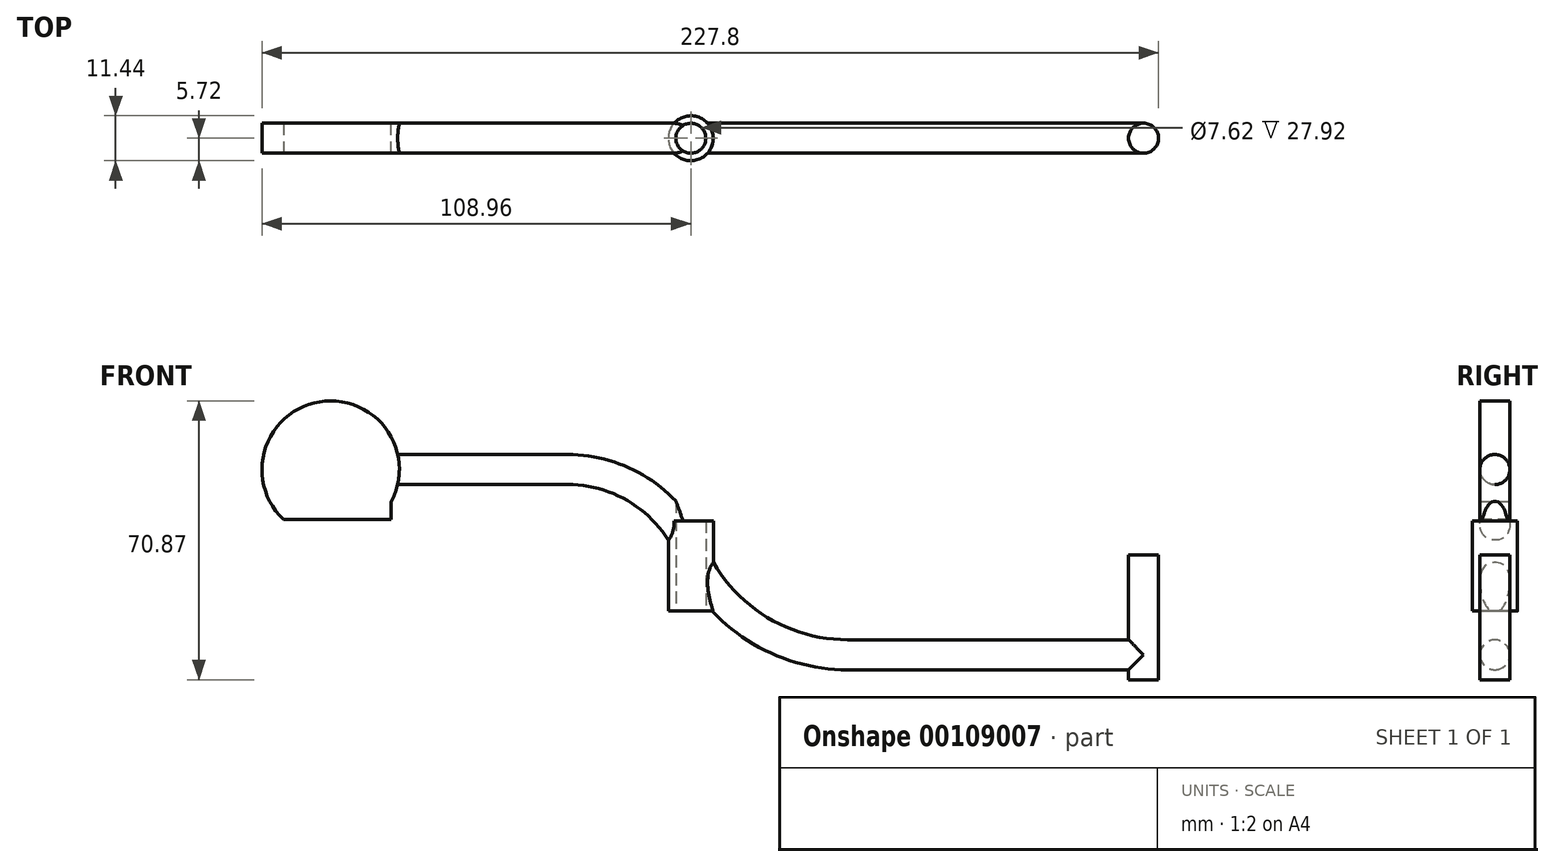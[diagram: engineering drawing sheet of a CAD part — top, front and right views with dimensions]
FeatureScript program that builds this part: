
annotation { "Feature Type Name" : "Feature", "Feature Type Description" : "" }
export const myFeature = defineFeature(function(context is Context, id is Id, definition is map)
    precondition{}
    {
        {
            var Q0;
            Q0=qCreatedBy(makeId("Front.planeOp"),FACE);
            var sketch = newSketch(context, id + "F0", { "sketchPlane" : qUnion([Q0])});
            skLineSegment(sketch, "E0", {"start": v(-106.83, 20.7) * mm, "end": v(-31.27, 20.7) * mm});
            skArc(sketch, "E1", {"start": v(-31.27, 20.7) * mm, "mid": v(-12.52, 15.05) * mm, "end": v(0, 0) * mm});
            skArc(sketch, "E2", {"start": v(0, 0) * mm, "mid": v(15.95, -19.18) * mm, "end": v(39.84, -26.37) * mm});
            skLineSegment(sketch, "E3", {"start": v(39.84, -26.37) * mm, "end": v(115.03, -26.37) * mm});
            skSolve(sketch);
        }
        {
            var Q0;
            Q0=sQuery(id+"F0.wireOp",EDGE,"E0");
            var Q1;
            Q1=sQuery(id+"F0.wireOp",VERTEX,"E0.start");
            cPlane(context, id + "F1", {"entities" : qUnion([Q0, Q1]), "cplaneType" : CPlaneType.LINE_POINT, "offset" : 25.4 * mm, "width" : 152.4 * mm, "height" : 152.4 * mm});
        }
        {
            var Q0;
            Q0=qCreatedBy(id+"F1.planeOp",FACE);
            var sketch = newSketch(context, id + "F2", { "sketchPlane" : qUnion([Q0])});
            skCircle(sketch, "E4", {"center": v(0, 20.7) * mm, "radius": 3.81 * mm});
            skSolve(sketch);
        }
        {
            var Q0;
            Q0=makeQuery(id+"F2.imprint","IMPRINT",FACE,{"disambiguationData":[TD([[makeQuery(id+"F2.imprint","IMPRINT",EDGE,{"derivedFrom":sQuery(id+"F2.wireOp",EDGE,"E4")}),1.0]])]});
            var Q1;
            Q1=sQuery(id+"F0.wireOp",EDGE,"E0");
            var Q2;
            Q2=sQuery(id+"F0.wireOp",EDGE,"E1");
            var Q3;
            Q3=sQuery(id+"F0.wireOp",EDGE,"E2");
            var Q4;
            Q4=sQuery(id+"F0.wireOp",EDGE,"E3");
            sweep(context, id + "F3", {"profiles" : qUnion([Q0]), "path" : qUnion([Q1, Q2, Q3, Q4])});
        }
        {
            var Q0;
            Q0=qCreatedBy(makeId("Top.planeOp"),FACE);
            var sketch = newSketch(context, id + "F4", { "sketchPlane" : qUnion([Q0])});
            skCircle(sketch, "E5", {"center": v(0, 0) * mm, "radius": 3.81 * mm});
            skCircle(sketch, "E6", {"center": v(0, 0) * mm, "radius": 5.72 * mm});
            skSolve(sketch);
        }
        {
            var Q0;
            Q0=makeQuery(id+"F4.imprint","IMPRINT",FACE,{"disambiguationData":[TD([[makeQuery(id+"F4.imprint","IMPRINT",EDGE,{"derivedFrom":sQuery(id+"F4.wireOp",EDGE,"E5")}),1.0]])]});
            extrude(context, id + "F5", {"entities" : qUnion([Q0]), "operationType" : NewBodyOperationType.REMOVE, "depth" : 25.4 * mm, "hasSecondDirection" : true, "secondDirectionOppositeDirection" : true, "secondDirectionDepth" : 25.4 * mm});
        }
        {
            var Q0;
            Q0=makeQuery(id+"F4.imprint","IMPRINT",FACE,{"disambiguationData":[TD([[makeQuery(id+"F4.imprint","IMPRINT",EDGE,{"derivedFrom":sQuery(id+"F4.wireOp",EDGE,"E5")}),-1.0]])]});
            extrude(context, id + "F6", {"entities" : qUnion([Q0]), "operationType" : NewBodyOperationType.ADD, "depth" : 7.62 * mm, "hasSecondDirection" : true, "secondDirectionOppositeDirection" : true, "secondDirectionDepth" : 15.24 * mm});
        }
        {
            var Q0;
            Q0=sQuery(id+"F0.wireOp",EDGE,"E3");
            cPlane(context, id + "F7", {"entities" : qUnion([Q0]), "cplaneType" : CPlaneType.LINE_ANGLE, "offset" : 25.4 * mm, "angle" : 90 * degree, "width" : 152.4 * mm, "height" : 152.4 * mm});
        }
        {
            var Q0;
            Q0=qCreatedBy(id+"F7.planeOp",FACE);
            var sketch = newSketch(context, id + "F8", { "sketchPlane" : qUnion([Q0])});
            skCircle(sketch, "E7", {"center": v(115.03, 0) * mm, "radius": 3.81 * mm});
            skSolve(sketch);
        }
        {
            var Q0;
            Q0=makeQuery(id+"F8.imprint","IMPRINT",FACE,{"disambiguationData":[TD([[makeQuery(id+"F8.imprint","IMPRINT",EDGE,{"derivedFrom":sQuery(id+"F8.wireOp",EDGE,"E7")}),1.0]])]});
            extrude(context, id + "F9", {"entities" : qUnion([Q0]), "operationType" : NewBodyOperationType.ADD, "depth" : 25.4 * mm, "hasSecondDirection" : true, "secondDirectionOppositeDirection" : true, "secondDirectionDepth" : 6.35 * mm});
        }
        {
            var Q0;
            Q0=qCreatedBy(makeId("Front.planeOp"),FACE);
            var sketch = newSketch(context, id + "F10", { "sketchPlane" : qUnion([Q0])});
            skLineSegment(sketch, "E8", {"start": v(-76.08, 20.7) * mm, "end": v(-76.08, 33.4) * mm});
            skLineSegment(sketch, "E9", {"start": v(-76.08, 33.4) * mm, "end": v(-106.91, 33.4) * mm});
            skLineSegment(sketch, "E10", {"start": v(-106.91, 33.4) * mm, "end": v(-106.91, 8) * mm});
            skLineSegment(sketch, "E11", {"start": v(-106.91, 8) * mm, "end": v(-76.08, 8) * mm});
            skLineSegment(sketch, "E12", {"start": v(-76.08, 8) * mm, "end": v(-76.08, 20.7) * mm});
            skSolve(sketch);
        }
        {
            var Q0;
            Q0=makeQuery(id+"F10.imprint","IMPRINT",FACE,{"disambiguationData":[TD([[makeQuery(id+"F10.imprint","IMPRINT",EDGE,{"derivedFrom":sQuery(id+"F10.wireOp",EDGE,"E8")}),1.0]])]});
            extrude(context, id + "F11", {"entities" : qUnion([Q0]), "operationType" : NewBodyOperationType.ADD, "depth" : 3.8 * mm, "hasSecondDirection" : true, "secondDirectionOppositeDirection" : true, "secondDirectionDepth" : 3.8 * mm});
        }
        {
            var Q0;
            Q0=makeQuery(id+"F11.opExtrude","CAP_FACE",FACE,{"disambiguationData":[OSD([sQuery(id+"F10.wireOp",EDGE,"E8"),sQuery(id+"F10.wireOp",EDGE,"E9"),sQuery(id+"F10.wireOp",EDGE,"E10"),sQuery(id+"F10.wireOp",EDGE,"E11"),sQuery(id+"F10.wireOp",EDGE,"E12")])],"isStart":false});
            var sketch = newSketch(context, id + "F12", { "sketchPlane" : qUnion([Q0])});
            skCircle(sketch, "E13", {"center": v(-91.5, 20.7) * mm, "radius": 17.46 * mm});
            skSolve(sketch);
        }
        {
            var Q0;
            {var subQ0=sQuery(id+"F12.wireOp",EDGE,"E13");var subQ1=makeQuery(id+"F11.opExtrude","CAP_EDGE",EDGE,{"disambiguationData":[OSD([sQuery(id+"F10.wireOp",EDGE,"E9")])],"isStart":false});var subQ2=makeQuery(id+"F12.imprint","INTERSECT",VERTEX,{"disambiguationData":[OD(0.0)],"derivedFrom":[subQ1,subQ0]});Q0=makeQuery(id+"F12.imprint","IMPRINT",FACE,{"disambiguationData":[TD([[makeQuery(id+"F12.imprint","IMPRINT",EDGE,{"disambiguationData":[TD([[subQ2,-1.0]])],"derivedFrom":subQ0}),1.0]])]});}
            var Q1;
            {var subQ0=sQuery(id+"F12.wireOp",EDGE,"E13");var subQ2=sQuery(id+"F10.wireOp",EDGE,"E12");var subQ4=sQuery(id+"F10.wireOp",EDGE,"E9");var subQ5=sQuery(id+"F10.wireOp",EDGE,"E8");var subQ8=makeQuery(id+"F11.opExtrude","CAP_EDGE",EDGE,{"disambiguationData":[OSD([subQ5,subQ2])],"isStart":false});var subQ9=makeQuery(id+"F11.boolean.opBoolean","SPLIT",EDGE,{"disambiguationData":[TD([makeQuery(id+"F11.opExtrude","SWEPT_FACE",FACE,{"disambiguationData":[OSD([subQ4])]})])],"derivedFrom":subQ8});var subQ10=makeQuery(id+"F12.imprint","INTERSECT",VERTEX,{"derivedFrom":[subQ9,subQ0]});Q1=makeQuery(id+"F12.imprint","IMPRINT",FACE,{"disambiguationData":[TD([[makeQuery(id+"F12.imprint","IMPRINT",EDGE,{"disambiguationData":[TD([[subQ10,1.0]])],"derivedFrom":subQ0}),1.0]])]});}
            var Q2;
            {var subQ0=sQuery(id+"F12.wireOp",EDGE,"E13");var subQ1=makeQuery(id+"F11.opExtrude","CAP_EDGE",EDGE,{"disambiguationData":[OSD([sQuery(id+"F10.wireOp",EDGE,"E11")])],"isStart":false});var subQ2=makeQuery(id+"F12.imprint","INTERSECT",VERTEX,{"disambiguationData":[OD(0.0)],"derivedFrom":[subQ1,subQ0]});Q2=makeQuery(id+"F12.imprint","IMPRINT",FACE,{"disambiguationData":[TD([[makeQuery(id+"F12.imprint","IMPRINT",EDGE,{"disambiguationData":[TD([[subQ2,-1.0]])],"derivedFrom":subQ0}),1.0]])]});}
            var Q3;
            {var subQ0=sQuery(id+"F12.wireOp",EDGE,"E13");var subQ1=makeQuery(id+"F11.opExtrude","CAP_EDGE",EDGE,{"disambiguationData":[OSD([sQuery(id+"F10.wireOp",EDGE,"E10")])],"isStart":false});var subQ2=makeQuery(id+"F12.imprint","INTERSECT",VERTEX,{"disambiguationData":[OD(0.0)],"derivedFrom":[subQ1,subQ0]});Q3=makeQuery(id+"F12.imprint","IMPRINT",FACE,{"disambiguationData":[TD([[makeQuery(id+"F12.imprint","IMPRINT",EDGE,{"disambiguationData":[TD([[subQ2,-1.0]])],"derivedFrom":subQ0}),1.0]])]});}
            extrude(context, id + "F13", {"entities" : qUnion([Q0, Q1, Q2, Q3]), "operationType" : NewBodyOperationType.ADD, "oppositeDirection" : true, "depth" : 7.62 * mm});
        }
        {
            var Q0;
            {var subQ0=sQuery(id+"F12.wireOp",EDGE,"E13");var subQ1=makeQuery(id+"F11.opExtrude","CAP_EDGE",EDGE,{"disambiguationData":[OSD([sQuery(id+"F10.wireOp",EDGE,"E9")])],"isStart":false});var subQ2=makeQuery(id+"F12.imprint","INTERSECT",VERTEX,{"disambiguationData":[OD(1.0)],"derivedFrom":[subQ1,subQ0]});Q0=makeQuery(id+"F12.imprint","IMPRINT",FACE,{"disambiguationData":[TD([[makeQuery(id+"F12.imprint","IMPRINT",EDGE,{"disambiguationData":[TD([[subQ2,-1.0]])],"derivedFrom":subQ0}),-1.0]])]});}
            var Q1;
            {var subQ0=sQuery(id+"F12.wireOp",EDGE,"E13");var subQ1=sQuery(id+"F10.wireOp",EDGE,"E9");var subQ2=makeQuery(id+"F11.opExtrude","CAP_EDGE",EDGE,{"disambiguationData":[OSD([subQ1])],"isStart":false});var subQ3=makeQuery(id+"F12.imprint","INTERSECT",VERTEX,{"disambiguationData":[OD(0.0)],"derivedFrom":[subQ2,subQ0]});Q1=makeQuery(id+"F12.imprint","IMPRINT",FACE,{"disambiguationData":[TD([[makeQuery(id+"F12.imprint","IMPRINT",EDGE,{"disambiguationData":[TD([[subQ3,1.0]])],"derivedFrom":subQ0}),-1.0]])]});}
            var Q2;
            {var subQ0=sQuery(id+"F12.wireOp",EDGE,"E13");var subQ1=sQuery(id+"F10.wireOp",EDGE,"E11");var subQ2=makeQuery(id+"F11.opExtrude","CAP_EDGE",EDGE,{"disambiguationData":[OSD([subQ1])],"isStart":false});var subQ3=makeQuery(id+"F12.imprint","INTERSECT",VERTEX,{"disambiguationData":[OD(1.0)],"derivedFrom":[subQ2,subQ0]});Q2=makeQuery(id+"F12.imprint","IMPRINT",FACE,{"disambiguationData":[TD([[makeQuery(id+"F12.imprint","IMPRINT",EDGE,{"disambiguationData":[TD([[subQ3,-1.0]])],"derivedFrom":subQ0}),-1.0]])]});}
            var Q3;
            {var subQ0=sQuery(id+"F12.wireOp",EDGE,"E13");var subQ1=makeQuery(id+"F11.opExtrude","CAP_EDGE",EDGE,{"disambiguationData":[OSD([sQuery(id+"F10.wireOp",EDGE,"E10")])],"isStart":false});var subQ2=makeQuery(id+"F12.imprint","INTERSECT",VERTEX,{"disambiguationData":[OD(1.0)],"derivedFrom":[subQ1,subQ0]});Q3=makeQuery(id+"F12.imprint","IMPRINT",FACE,{"disambiguationData":[TD([[makeQuery(id+"F12.imprint","IMPRINT",EDGE,{"disambiguationData":[TD([[subQ2,-1.0]])],"derivedFrom":subQ0}),-1.0]])]});}
            extrude(context, id + "F14", {"entities" : qUnion([Q0, Q1, Q2, Q3]), "operationType" : NewBodyOperationType.REMOVE, "oppositeDirection" : true, "depth" : 25.4 * mm});
        }
    });
